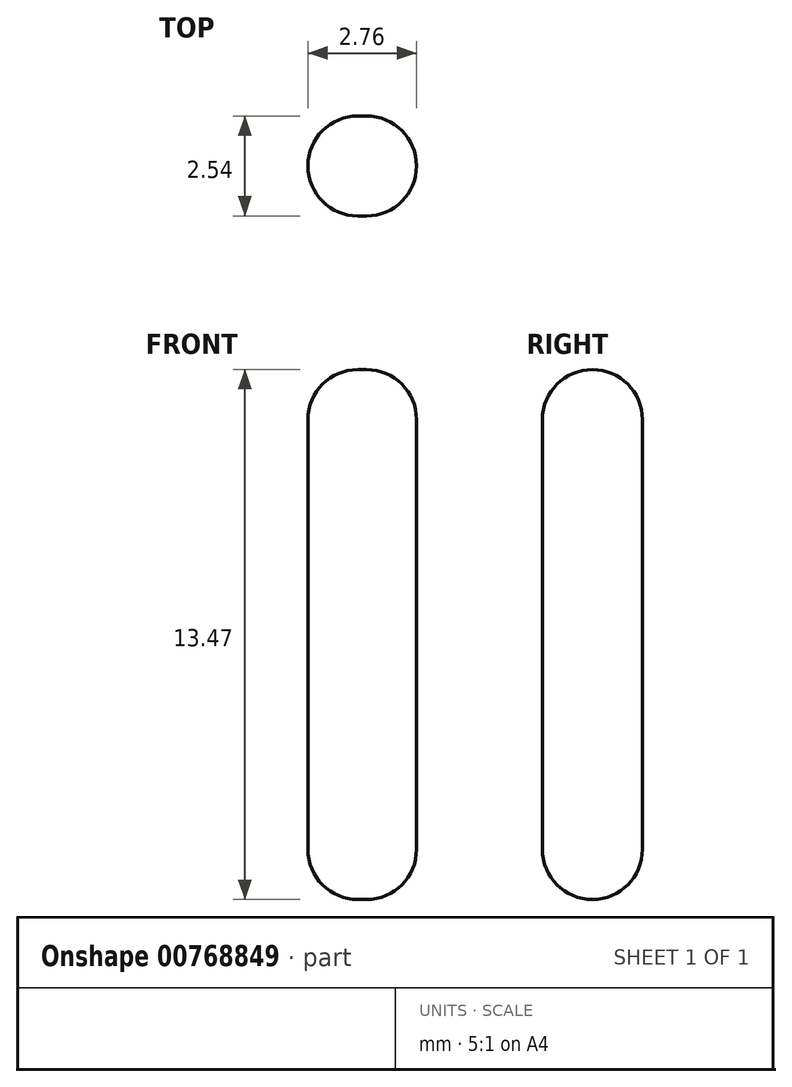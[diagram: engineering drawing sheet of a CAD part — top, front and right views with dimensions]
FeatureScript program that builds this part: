
annotation { "Feature Type Name" : "Feature", "Feature Type Description" : "" }
export const myFeature = defineFeature(function(context is Context, id is Id, definition is map)
    precondition{}
    {
        {
            var Q0;
            Q0=qCreatedBy(makeId("Front.planeOp"),FACE);
            var sketch = newSketch(context, id + "F0", { "sketchPlane" : qUnion([Q0])});
            skLineSegment(sketch, "E0.bottom", {"start": v(-56.53, 46.6) * mm, "end": v(-53.77, 46.6) * mm});
            skLineSegment(sketch, "E0.top", {"start": v(-56.53, 33.13) * mm, "end": v(-53.77, 33.13) * mm});
            skLineSegment(sketch, "E0.left", {"start": v(-56.53, 46.6) * mm, "end": v(-56.53, 33.13) * mm});
            skLineSegment(sketch, "E0.right", {"start": v(-53.77, 46.6) * mm, "end": v(-53.77, 33.13) * mm});
            skSolve(sketch);
        }
        {
            var Q0;
            Q0 = qSketchRegion(id + "F0", true);
            extrude(context, id + "F1", {"entities" : qUnion([Q0]), "depth" : 2.54 * mm, "offsetDistance" : 25.4 * mm});
        }
        {
            var Q0;
            Q0=makeQuery(id+"F1.opExtrude","CAP_EDGE",EDGE,{"disambiguationData":[OSD([sQuery(id+"F0.wireOp",EDGE,"E0.bottom")])],"isStart":false});
            var Q1;
            Q1=makeQuery(id+"F1.opExtrude","CAP_EDGE",EDGE,{"disambiguationData":[OSD([sQuery(id+"F0.wireOp",EDGE,"E0.right")])],"isStart":false});
            var Q2;
            Q2=makeQuery(id+"F1.opExtrude","CAP_EDGE",EDGE,{"disambiguationData":[OSD([sQuery(id+"F0.wireOp",EDGE,"E0.left")])],"isStart":false});
            var Q3;
            Q3=makeQuery(id+"F1.opExtrude","CAP_EDGE",EDGE,{"disambiguationData":[OSD([sQuery(id+"F0.wireOp",EDGE,"E0.top")])],"isStart":false});
            var Q4;
            Q4=makeQuery(id+"F1.opExtrude","CAP_EDGE",EDGE,{"disambiguationData":[OSD([sQuery(id+"F0.wireOp",EDGE,"E0.bottom")])],"isStart":true});
            var Q5;
            Q5=makeQuery(id+"F1.opExtrude","SWEPT_EDGE",EDGE,{"disambiguationData":[OSD([sQuery(id+"F0.wireOp",EDGE,"E0.bottom"),sQuery(id+"F0.wireOp",EDGE,"E0.right")])]});
            var Q6;
            Q6=makeQuery(id+"F1.opExtrude","SWEPT_EDGE",EDGE,{"disambiguationData":[OSD([sQuery(id+"F0.wireOp",EDGE,"E0.top"),sQuery(id+"F0.wireOp",EDGE,"E0.right")])]});
            var Q7;
            Q7=makeQuery(id+"F1.opExtrude","CAP_EDGE",EDGE,{"disambiguationData":[OSD([sQuery(id+"F0.wireOp",EDGE,"E0.right")])],"isStart":true});
            var Q8;
            Q8=makeQuery(id+"F1.opExtrude","CAP_EDGE",EDGE,{"disambiguationData":[OSD([sQuery(id+"F0.wireOp",EDGE,"E0.top")])],"isStart":true});
            var Q9;
            Q9=makeQuery(id+"F1.opExtrude","SWEPT_EDGE",EDGE,{"disambiguationData":[OSD([sQuery(id+"F0.wireOp",EDGE,"E0.bottom"),sQuery(id+"F0.wireOp",EDGE,"E0.left")])]});
            var Q10;
            Q10=makeQuery(id+"F1.opExtrude","SWEPT_EDGE",EDGE,{"disambiguationData":[OSD([sQuery(id+"F0.wireOp",EDGE,"E0.top"),sQuery(id+"F0.wireOp",EDGE,"E0.left")])]});
            fillet(context, id + "F2", {"entities" : qUnion([Q0, Q1, Q2, Q3, Q4, Q5, Q6, Q7, Q8, Q9, Q10]), "radius" : 1.27 * mm, "tangentPropagation" : true, "allowEdgeOverflow" : false});
        }
        {
            var Q0;
            Q0=makeQuery(id+"F1.opExtrude","CAP_EDGE",EDGE,{"disambiguationData":[OSD([sQuery(id+"F0.wireOp",EDGE,"E0.left")])],"isStart":true});
            fillet(context, id + "F3", {"entities" : qUnion([Q0]), "radius" : 1.27 * mm, "tangentPropagation" : true, "allowEdgeOverflow" : false});
        }
    });
